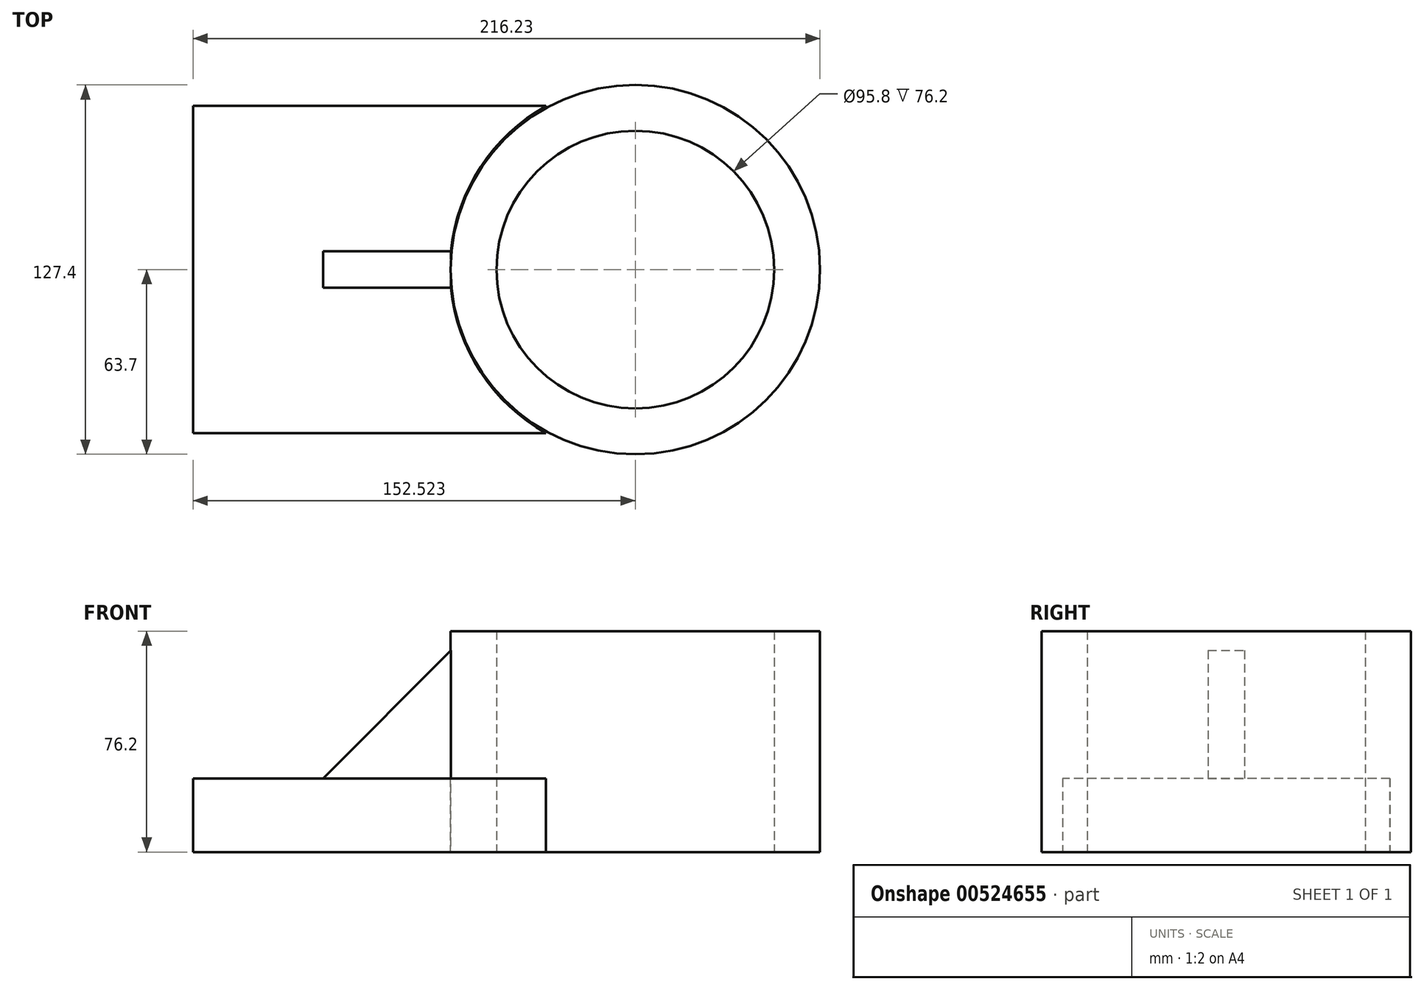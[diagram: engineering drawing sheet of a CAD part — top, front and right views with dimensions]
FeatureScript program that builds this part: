
annotation { "Feature Type Name" : "Feature", "Feature Type Description" : "" }
export const myFeature = defineFeature(function(context is Context, id is Id, definition is map)
    precondition{}
    {
        {
            var Q0;
            Q0=qCreatedBy(makeId("Top.planeOp"),FACE);
            var sketch = newSketch(context, id + "F0", { "sketchPlane" : qUnion([Q0])});
            skLineSegment(sketch, "E0.bottom", {"start": v(-76.57, 56.45) * mm, "end": v(45.16, 56.45) * mm});
            skLineSegment(sketch, "E0.top", {"start": v(-76.57, -56.45) * mm, "end": v(45.16, -56.45) * mm});
            skLineSegment(sketch, "E0.left", {"start": v(-76.57, 56.45) * mm, "end": v(-76.57, -56.45) * mm});
            skLineSegment(sketch, "E0.right", {"start": v(45.16, 56.45) * mm, "end": v(45.16, -56.45) * mm});
            skCircle(sketch, "E1", {"center": v(76.57, 0) * mm, "radius": 64.53 * mm});
            skCircle(sketch, "E2", {"center": v(76.57, 0) * mm, "radius": 45.48 * mm});
            skSolve(sketch);
        }
        {
            var Q0;
            {var subQ1=sQuery(id+"F0.wireOp",EDGE,"E0.bottom");Q0=makeQuery(id+"F0.imprint","IMPRINT",FACE,{"disambiguationData":[TD([[makeQuery(id+"F0.imprint","IMPRINT",EDGE,{"derivedFrom":subQ1}),-1.0]])]});}
            extrude(context, id + "F1", {"entities" : qUnion([Q0]), "depth" : 25.4 * mm, "offsetDistance" : 25.4 * mm});
        }
        {
            var Q0;
            Q0=qCreatedBy(makeId("Top.planeOp"),FACE);
            var sketch = newSketch(context, id + "F2", { "sketchPlane" : qUnion([Q0])});
            skCircle(sketch, "E3", {"center": v(75.95, 0) * mm, "radius": 63.7 * mm});
            skCircle(sketch, "E4", {"center": v(75.95, 0) * mm, "radius": 47.9 * mm});
            skSolve(sketch);
        }
        {
            var Q0;
            Q0=makeQuery(id+"F2.imprint","IMPRINT",FACE,{"disambiguationData":[TD([[makeQuery(id+"F2.imprint","IMPRINT",EDGE,{"derivedFrom":sQuery(id+"F2.wireOp",EDGE,"E3")}),1.0]])]});
            extrude(context, id + "F3", {"entities" : qUnion([Q0]), "depth" : 76.2 * mm, "offsetDistance" : 25.4 * mm});
        }
        {
            var Q0;
            Q0=makeQuery(id+"F1.opExtrude","CAP_FACE",FACE,{"disambiguationData":[OSD([sQuery(id+"F0.wireOp",EDGE,"E0.bottom"),sQuery(id+"F0.wireOp",EDGE,"E0.top"),sQuery(id+"F0.wireOp",EDGE,"E0.left"),sQuery(id+"F0.wireOp",EDGE,"E0.right"),sQuery(id+"F0.wireOp",EDGE,"E1")])],"isStart":false});
            var sketch = newSketch(context, id + "F4", { "sketchPlane" : qUnion([Q0])});
            skLineSegment(sketch, "E5.bottom", {"start": v(12.35, -6.32) * mm, "end": v(-53.33, -6.32) * mm});
            skLineSegment(sketch, "E5.top", {"start": v(12.35, 6.32) * mm, "end": v(-53.33, 6.32) * mm});
            skLineSegment(sketch, "E5.left", {"start": v(12.35, -6.32) * mm, "end": v(12.35, 6.32) * mm});
            skLineSegment(sketch, "E5.right", {"start": v(-53.33, -6.32) * mm, "end": v(-53.33, 6.32) * mm});
            skPoint(sketch, "E5.middle", {"position": v(-20.5, 0) * mm});
            skSolve(sketch);
        }
        {
            var Q0;
            {var subQ0=sQuery(id+"F4.wireOp",EDGE,"E5.left");Q0=makeQuery(id+"F4.imprint","IMPRINT",FACE,{"disambiguationData":[TD([[makeQuery(id+"F4.imprint","IMPRINT",EDGE,{"derivedFrom":subQ0}),1.0]])]});}
            var Q1;
            {var subQ0=sQuery(id+"F4.wireOp",EDGE,"E5.bottom");Q1=makeQuery(id+"F4.imprint","IMPRINT",FACE,{"disambiguationData":[TD([[makeQuery(id+"F4.imprint","IMPRINT",EDGE,{"derivedFrom":subQ0}),-1.0]])]});}
            extrude(context, id + "F5", {"entities" : qUnion([Q0, Q1]), "depth" : 44.45 * mm, "offsetDistance" : 25.4 * mm});
        }
        {
            var Q0;
            Q0=makeQuery(id+"F5.opExtrude","CAP_EDGE",EDGE,{"disambiguationData":[OSD([sQuery(id+"F4.wireOp",EDGE,"E5.right")])],"isStart":false});
            chamfer(context, id + "F6", {"entities" : qUnion([Q0]), "width" : 66.04 * mm, "tangentPropagation" : true});
        }
    });
